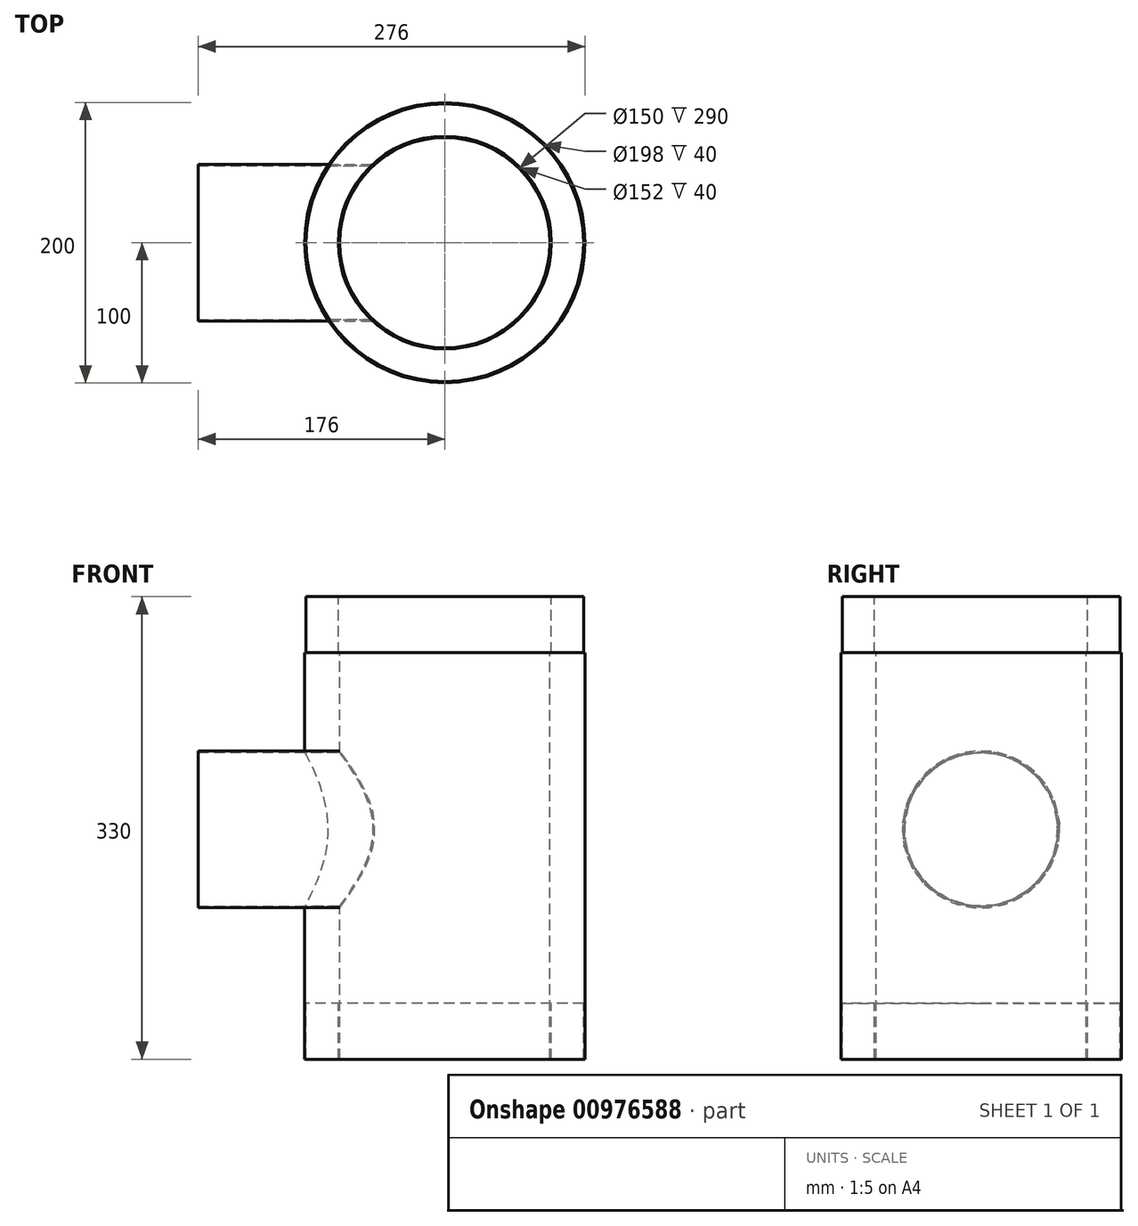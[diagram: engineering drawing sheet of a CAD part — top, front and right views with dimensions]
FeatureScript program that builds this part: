
annotation { "Feature Type Name" : "Feature", "Feature Type Description" : "" }
export const myFeature = defineFeature(function(context is Context, id is Id, definition is map)
    precondition{}
    {
        {
            var Q0;
            Q0=qCreatedBy(makeId("Front.planeOp"),FACE);
            var sketch = newSketch(context, id + "F0", { "sketchPlane" : qUnion([Q0])});
            skLineSegment(sketch, "E0", {"start": v(0, 722.18) * mm, "end": v(0, -793.11) * mm, "construction": true});
            skLineSegment(sketch, "E1", {"start": v(-75, -164) * mm, "end": v(-75, 126) * mm});
            skLineSegment(sketch, "E2", {"start": v(-75, 126) * mm, "end": v(-76, 126) * mm});
            skLineSegment(sketch, "E3", {"start": v(-76, 126) * mm, "end": v(-76, 166) * mm});
            skLineSegment(sketch, "E4", {"start": v(-76, 166) * mm, "end": v(-99, 166) * mm});
            skLineSegment(sketch, "E5", {"start": v(-99, 166) * mm, "end": v(-99, 126) * mm});
            skLineSegment(sketch, "E6", {"start": v(-99, 126) * mm, "end": v(-100, 126) * mm});
            skLineSegment(sketch, "E7", {"start": v(-100, 126) * mm, "end": v(-100, -164) * mm});
            skLineSegment(sketch, "E8", {"start": v(-100, -164) * mm, "end": v(-99, -164) * mm});
            skLineSegment(sketch, "E9", {"start": v(-99, -164) * mm, "end": v(-99, -124) * mm});
            skLineSegment(sketch, "E10", {"start": v(-99, -124) * mm, "end": v(-76, -124) * mm});
            skLineSegment(sketch, "E11", {"start": v(-76, -124) * mm, "end": v(-76, -164) * mm});
            skLineSegment(sketch, "E12", {"start": v(-76, -164) * mm, "end": v(-75, -164) * mm});
            skLineSegment(sketch, "E13", {"start": v(0, 0) * mm, "end": v(-350, 0) * mm, "construction": true});
            skLineSegment(sketch, "E14", {"start": v(0, -55) * mm, "end": v(-176, -55) * mm});
            skLineSegment(sketch, "E15", {"start": v(-176, -55) * mm, "end": v(-176, -56) * mm});
            skLineSegment(sketch, "E16", {"start": v(-176, -56) * mm, "end": v(0, -56) * mm});
            skLineSegment(sketch, "E17", {"start": v(0, -56) * mm, "end": v(0, -55) * mm});
            skLineSegment(sketch, "E18", {"start": v(-176, 0) * mm, "end": v(-175, 0) * mm});
            skSolve(sketch);
        }
        {
            var Q0;
            {var subQ0=sQuery(id+"F0.wireOp",EDGE,"E2");Q0=makeQuery(id+"F0.imprint","IMPRINT",FACE,{"disambiguationData":[TD([[makeQuery(id+"F0.imprint","IMPRINT",EDGE,{"derivedFrom":subQ0}),1.0]])]});}
            var Q1;
            {var subQ0=sQuery(id+"F0.wireOp",EDGE,"E16");var subQ1=sQuery(id+"F0.wireOp",EDGE,"E1");var subQ2=makeQuery(id+"F0.imprint","INTERSECT",VERTEX,{"derivedFrom":[subQ1,subQ0]});Q1=makeQuery(id+"F0.imprint","IMPRINT",FACE,{"disambiguationData":[TD([[makeQuery(id+"F0.imprint","IMPRINT",EDGE,{"disambiguationData":[TD([[subQ2,-1.0]])],"derivedFrom":subQ1}),1.0]])]});}
            var Q2;
            {var subQ0=sQuery(id+"F0.wireOp",EDGE,"E8");Q2=makeQuery(id+"F0.imprint","IMPRINT",FACE,{"disambiguationData":[TD([[makeQuery(id+"F0.imprint","IMPRINT",EDGE,{"derivedFrom":subQ0}),1.0]])]});}
            var Q3;
            Q3=sQuery(id+"F0.wireOp",EDGE,"E0");
            revolve(context, id + "F1", {"entities" : qUnion([Q0, Q1, Q2]), "axis" : qUnion([Q3]), "revolveType" : RevolveType.FULL});
        }
        {
            var Q0;
            {var subQ0=sQuery(id+"F0.wireOp",EDGE,"w0J2LYEv-GRHg-aT9r-p4lJ-qIvym3v4zpzr");Q0=makeQuery(id+"F0.imprint","IMPRINT",FACE,{"disambiguationData":[TD([[makeQuery(id+"F0.imprint","IMPRINT",EDGE,{"derivedFrom":subQ0}),-1.0]])]});}
            var Q1;
            {var subQ0=sQuery(id+"F0.wireOp",EDGE,"E15");Q1=makeQuery(id+"F0.imprint","IMPRINT",FACE,{"disambiguationData":[TD([[makeQuery(id+"F0.imprint","IMPRINT",EDGE,{"derivedFrom":subQ0}),1.0]])]});}
            var Q2;
            {var subQ0=sQuery(id+"F0.wireOp",EDGE,"E16");var subQ1=sQuery(id+"F0.wireOp",EDGE,"E1");var subQ2=makeQuery(id+"F0.imprint","INTERSECT",VERTEX,{"derivedFrom":[subQ1,subQ0]});Q2=makeQuery(id+"F0.imprint","IMPRINT",FACE,{"disambiguationData":[TD([[makeQuery(id+"F0.imprint","IMPRINT",EDGE,{"disambiguationData":[TD([[subQ2,-1.0]])],"derivedFrom":subQ1}),1.0]])]});}
            var Q3;
            {var subQ5=sQuery(id+"F0.wireOp",EDGE,"E17");Q3=makeQuery(id+"F0.imprint","IMPRINT",FACE,{"disambiguationData":[TD([[makeQuery(id+"F0.imprint","IMPRINT",EDGE,{"derivedFrom":subQ5}),1.0]])]});}
            var Q4;
            Q4=sQuery(id+"F0.wireOp",EDGE,"E13");
            revolve(context, id + "F2", {"entities" : qUnion([Q0, Q1, Q2, Q3]), "axis" : qUnion([Q4]), "revolveType" : RevolveType.FULL});
        }
        {
            var Q0;
            Q0=makeQuery(id+"F2.opRevolve","SWEPT_FACE",FACE,{"disambiguationData":[OSD([sQuery(id+"F0.wireOp",EDGE,"E15"),sQuery(id+"F0.wireOp",EDGE,"w0J2LYEv-GRHg-aT9r-p4lJ-qIvym3v4zpzr")])]});
            var sketch = newSketch(context, id + "F3", { "sketchPlane" : qUnion([Q0])});
            skCircle(sketch, "E19", {"center": v(0, 0) * mm, "radius": 55 * mm});
            skSolve(sketch);
        }
        {
            var Q0;
            Q0=qSketchRegion(id+"F3",true);
            var Q1;
            Q1=makeQuery(id+"F2.opRevolve","SWEPT_FACE",FACE,{"disambiguationData":[OSD([sQuery(id+"F0.wireOp",EDGE,"E17")])]});
            extrude(context, id + "F4", {"entities" : qUnion([Q0]), "operationType" : NewBodyOperationType.REMOVE, "endBound" : BoundingType.UP_TO_SURFACE, "oppositeDirection" : true, "endBoundEntityFace" : qUnion([Q1]), "offsetDistance" : 25 * mm, "depth" : 600 * mm});
        }
        {
            var Q0;
            Q0=makeQuery(id+"F1.opRevolve","SWEPT_FACE",FACE,{"disambiguationData":[OSD([sQuery(id+"F0.wireOp",EDGE,"E4")])]});
            var sketch = newSketch(context, id + "F5", { "sketchPlane" : qUnion([Q0])});
            skCircle(sketch, "E20", {"center": v(0, 0) * mm, "radius": 75 * mm});
            skSolve(sketch);
        }
        {
            var Q0;
            Q0=qSketchRegion(id+"F5",true);
            extrude(context, id + "F6", {"entities" : qUnion([Q0]), "operationType" : NewBodyOperationType.REMOVE, "oppositeDirection" : true, "depth" : 1200 * mm});
        }
    });
